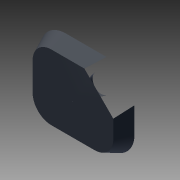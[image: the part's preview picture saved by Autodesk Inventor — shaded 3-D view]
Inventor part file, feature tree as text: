
AUTODESK INVENTOR PART (.ipt)
format: ipt  version: 2016 (Build 200138000, 138)  size: 270,848 bytes
history: native  units: in
note: dims shown in document units (in); Inventor stores cm internally (conversion verified against a paired STEP export)
features: other x2, extrude x1, imported_body x1
ambient origin geometry x8: Origin, YZ Plane, XZ Plane, XY Plane, X Axis, Y Axis, Z Axis, Center Point
bodies: Body1 (feature_tree)
feature tree (4):
  other  "Boss-Extrude3"
  other  "kinect base1"
  extrude  "Extrusion1"  Depth=0.001in TaperAngle=0.0deg
  imported_body  "Base1"
